# Revit family: Overhead-Sect_HAAS_Res_AmerTrad_Dbl
name_source: partatom
category: Doors
units: mm (PartAtom-declared; Revit-internal decimal feet)

## family parameters
Always vertical = Yes
Classification Number = 23.30.10.17.37.14
Cut with Voids When Loaded = No
Host = Wall
Room Calculation Point = No
Shared = No

## types (1)
- as Specified
    AAMA Designation = as Specified
    Assembly Code = B2030410
    Cost = 0 $
    Description = Haas American Traditions Series Residential Insulated Overhead Sectional Door - American Tradition Double Door as Specified
    End Stile Type = Steel
    Expected Lifespan (Years) = 0
    Exterior Skin = Woodgrain Steel
    Function = Exterior
    Height = 0' - 0"
    Interior Skin = Woodgrain Steel
    Keynote = 08360
    Maintenance Schedule (Months) = 0
    Manufacturer = Haas Door Co.
    Manufacturer Fax = 800-874-4227
    Manufacturer Website = http://www.haasdoor.com
    Max Height = 12' - 0"
    Max Width = 16' - 0"
    Model = American Tradition Double Door
    Operation = Overhead Sectional
    Panel Thickness = 0' - 3"
    Product Data = http://www.arcat.com
    R-Value = 13.45
    Revision = R1_2015-11
    Roof Incline Default = 0.00°
    Rough Height = 0' - 0"
    Rough Width = 0' - 0"
    Sales Information = http://www.haasdoor.com
    Standards Conformance = as Specified
    Thickness = 0' - 0"
    U Value = 0
    URL = http://www.haasdoor.com
    Wall Closure = By host
    Warranty Duration (Years) = 0
    Width = 0' - 0"
    rearspring = No

## geometry (parser evidence)
native form markers: Sweep x9
no freeform markers — native parametric forms only
